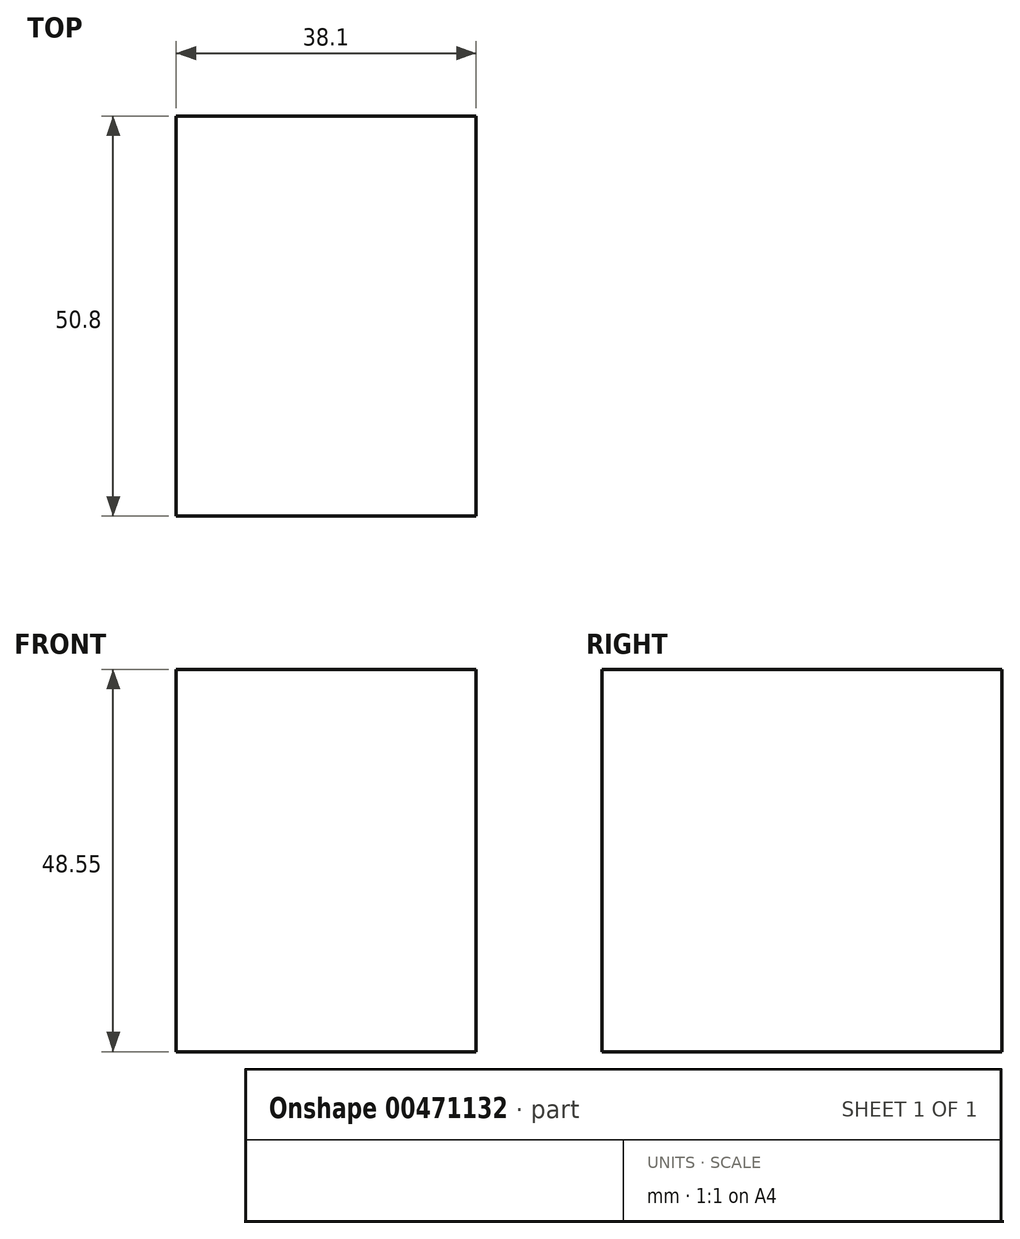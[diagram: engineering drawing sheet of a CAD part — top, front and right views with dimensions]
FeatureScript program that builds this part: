
annotation { "Feature Type Name" : "Feature", "Feature Type Description" : "" }
export const myFeature = defineFeature(function(context is Context, id is Id, definition is map)
    precondition{}
    {
        {
            var Q0;
            Q0=qCreatedBy(makeId("Front.planeOp"),FACE);
            var sketch = newSketch(context, id + "F0", { "sketchPlane" : qUnion([Q0])});
            skCircle(sketch, "E0", {"center": v(0, 0) * mm, "radius": 49.19 * mm});
            skLineSegment(sketch, "E1.bottom", {"start": v(-125.33, 14.15) * mm, "end": v(-87.23, 14.15) * mm});
            skLineSegment(sketch, "E1.top", {"start": v(-125.33, -34.4) * mm, "end": v(-87.23, -34.4) * mm});
            skLineSegment(sketch, "E1.left", {"start": v(-125.33, 14.15) * mm, "end": v(-125.33, -34.4) * mm});
            skLineSegment(sketch, "E1.right", {"start": v(-87.23, 14.15) * mm, "end": v(-87.23, -34.4) * mm});
            skSolve(sketch);
        }
        {
            var Q0;
            Q0=sQuery(id+"F0.wireOp",EDGE,"E1.top");
            var Q1;
            Q1=sQuery(id+"F0.wireOp",EDGE,"E1.left");
            var Q2;
            Q2=sQuery(id+"F0.wireOp",EDGE,"E1.bottom");
            var Q3;
            Q3=sQuery(id+"F0.wireOp",EDGE,"E1.right");
            extrude(context, id + "F1", {"bodyType" : ToolBodyType.SURFACE, "surfaceEntities" : qUnion([Q0, Q1, Q2, Q3]), "depth" : 50.8 * mm});
        }
    });
